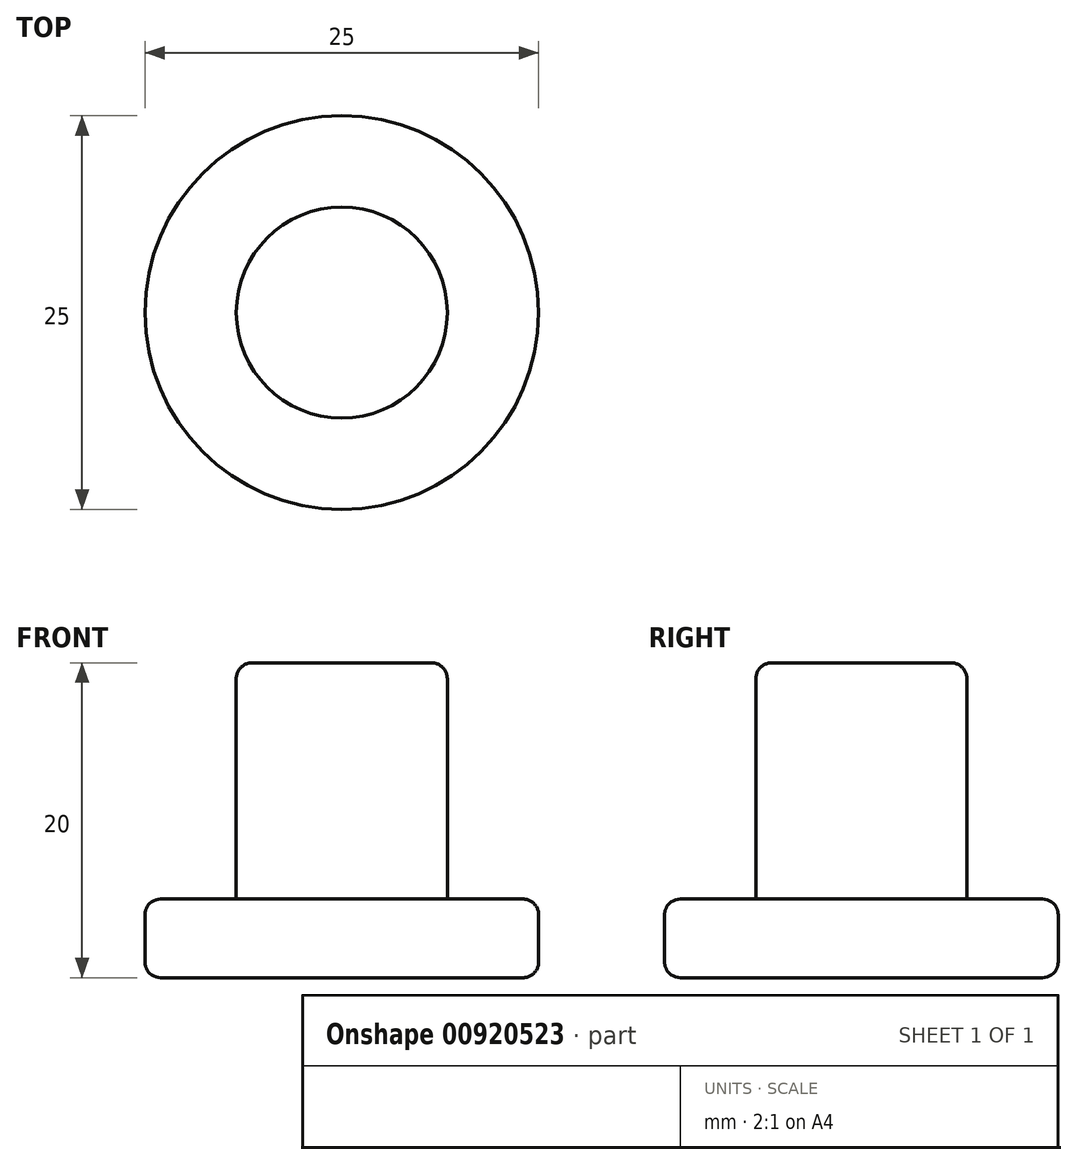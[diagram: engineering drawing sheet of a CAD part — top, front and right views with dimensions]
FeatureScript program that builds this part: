
annotation { "Feature Type Name" : "Feature", "Feature Type Description" : "" }
export const myFeature = defineFeature(function(context is Context, id is Id, definition is map)
    precondition{}
    {
        {
            var Q0;
            Q0=qCreatedBy(makeId("Top.planeOp"),FACE);
            var sketch = newSketch(context, id + "F0", { "sketchPlane" : qUnion([Q0])});
            skCircle(sketch, "E0", {"center": v(0, 0) * mm, "radius": 12.5 * mm});
            skSolve(sketch);
        }
        {
            var Q0;
            Q0=makeQuery(id+"F0.imprint","IMPRINT",FACE,{"disambiguationData":[TD([[makeQuery(id+"F0.imprint","IMPRINT",EDGE,{"derivedFrom":sQuery(id+"F0.wireOp",EDGE,"E0")}),1.0]])]});
            extrude(context, id + "F1", {"entities" : qUnion([Q0]), "depth" : 5 * mm, "offsetDistance" : 25 * mm});
        }
        {
            var Q0;
            Q0=makeQuery(id+"F1.opExtrude","CAP_FACE",FACE,{"disambiguationData":[OSD([sQuery(id+"F0.wireOp",EDGE,"E0")])],"isStart":true});
            var sketch = newSketch(context, id + "F2", { "sketchPlane" : qUnion([Q0])});
            skCircle(sketch, "E1", {"center": v(0, 0) * mm, "radius": 6.7 * mm});
            skSolve(sketch);
        }
        {
            var Q0;
            Q0=makeQuery(id+"F2.imprint","IMPRINT",FACE,{"disambiguationData":[TD([[makeQuery(id+"F2.imprint","IMPRINT",EDGE,{"derivedFrom":sQuery(id+"F2.wireOp",EDGE,"E1")}),1.0]])]});
            extrude(context, id + "F3", {"entities" : qUnion([Q0]), "operationType" : NewBodyOperationType.ADD, "oppositeDirection" : true, "depth" : 20 * mm, "offsetDistance" : 25 * mm});
        }
        {
            var Q0;
            Q0=makeQuery(id+"F1.opExtrude","CAP_EDGE",EDGE,{"disambiguationData":[OSD([sQuery(id+"F0.wireOp",EDGE,"E0")])],"isStart":true});
            var Q1;
            Q1=makeQuery(id+"F1.opExtrude","CAP_EDGE",EDGE,{"disambiguationData":[OSD([sQuery(id+"F0.wireOp",EDGE,"E0")])],"isStart":false});
            var Q2;
            Q2=makeQuery(id+"F3.opExtrude","CAP_EDGE",EDGE,{"disambiguationData":[OSD([sQuery(id+"F2.wireOp",EDGE,"E1")])],"isStart":false});
            fillet(context, id + "F4", {"entities" : qUnion([Q0, Q1, Q2]), "radius" : 1 * mm, "tangentPropagation" : true, "allowEdgeOverflow" : false});
        }
    });
